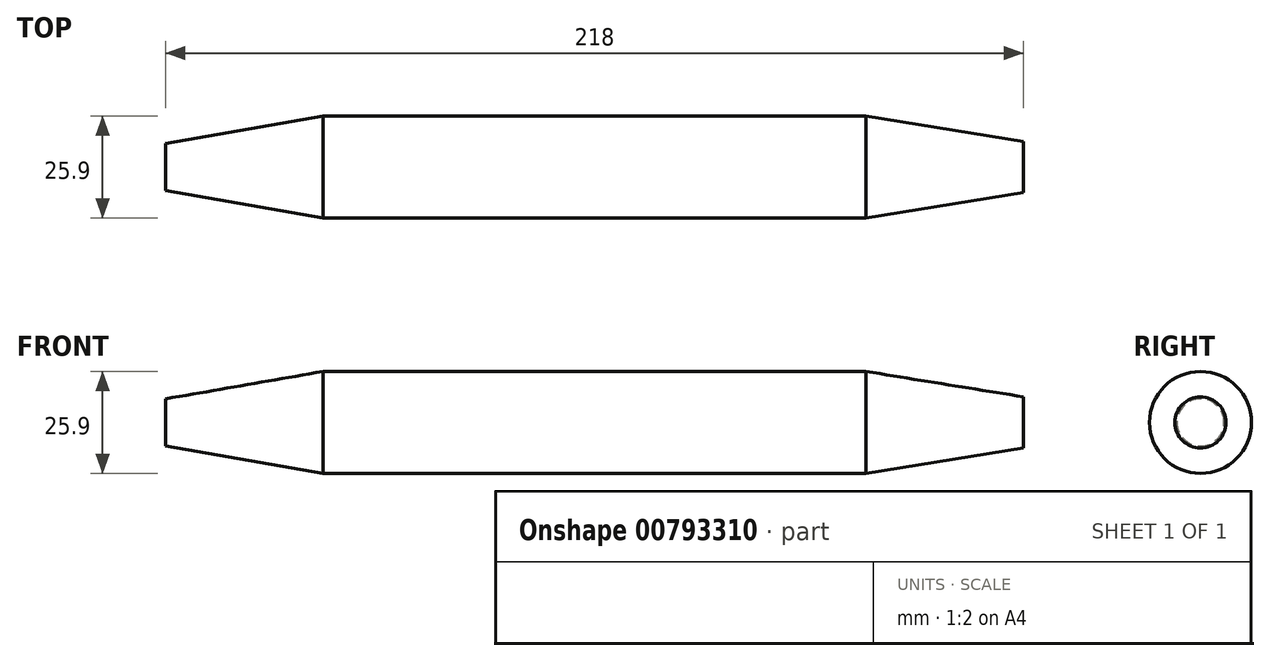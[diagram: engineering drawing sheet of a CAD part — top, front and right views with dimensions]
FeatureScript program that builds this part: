
annotation { "Feature Type Name" : "Feature", "Feature Type Description" : "" }
export const myFeature = defineFeature(function(context is Context, id is Id, definition is map)
    precondition{}
    {
        {
            var Q0;
            Q0=qCreatedBy(makeId("Front.planeOp"),FACE);
            var sketch = newSketch(context, id + "F0", { "sketchPlane" : qUnion([Q0])});
            skLineSegment(sketch, "E0", {"start": v(0, 0) * mm, "end": v(0, 6) * mm});
            skLineSegment(sketch, "E1", {"start": v(40, 12.95) * mm, "end": v(0, 6) * mm});
            skLineSegment(sketch, "E2", {"start": v(40, 12.95) * mm, "end": v(178, 12.95) * mm});
            skLineSegment(sketch, "E3", {"start": v(218, 0) * mm, "end": v(218, 6.5) * mm});
            skLineSegment(sketch, "E4", {"start": v(218, 6.5) * mm, "end": v(178, 12.95) * mm});
            skLineSegment(sketch, "E5", {"start": v(0, 0) * mm, "end": v(218, 0) * mm});
            skSolve(sketch);
        }
        {
            var Q0;
            Q0 = qSketchRegion(id + "F0", true);
            var Q1;
            Q1=sQuery(id+"F0.wireOp",EDGE,"E5");
            revolve(context, id + "F1", {"surfaceOperationType" : NewSurfaceOperationType.NEW, "entities" : qUnion([Q0]), "axis" : qUnion([Q1]), "revolveType" : RevolveType.FULL});
        }
    });
